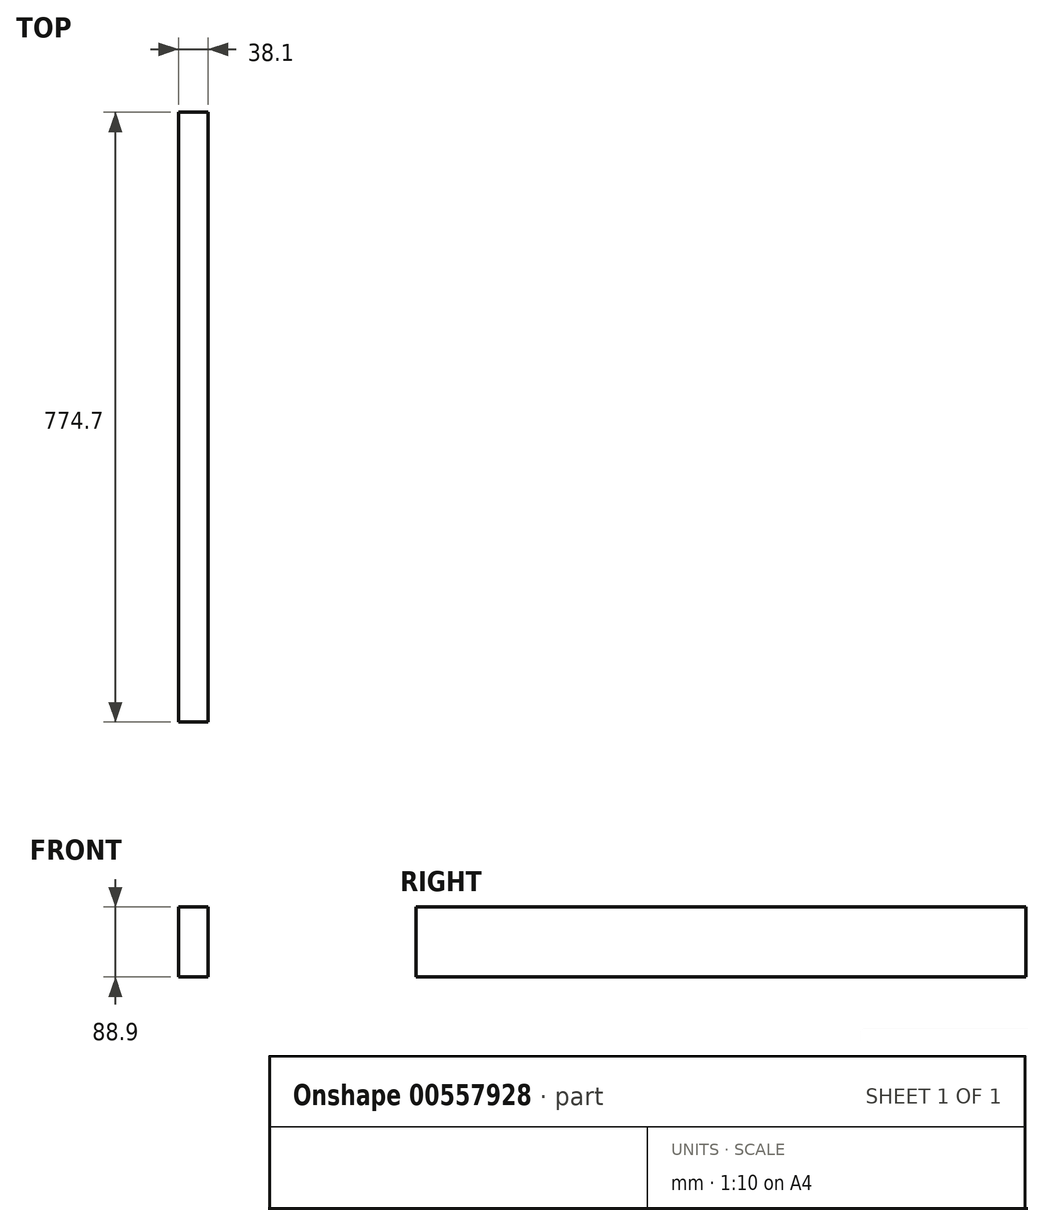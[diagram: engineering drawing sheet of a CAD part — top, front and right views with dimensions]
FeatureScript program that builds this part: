
annotation { "Feature Type Name" : "Feature", "Feature Type Description" : "" }
export const myFeature = defineFeature(function(context is Context, id is Id, definition is map)
    precondition{}
    {
        {
            var Q0;
            Q0=qCreatedBy(makeId("Right.planeOp"),FACE);
            var sketch = newSketch(context, id + "F0", { "sketchPlane" : qUnion([Q0])});
            skLineSegment(sketch, "E0.bottom", {"start": v(77.94, 175.26) * mm, "end": v(77.94, 86.36) * mm});
            skLineSegment(sketch, "E0.top", {"start": v(852.64, 175.26) * mm, "end": v(852.64, 86.36) * mm});
            skLineSegment(sketch, "E0.left", {"start": v(77.94, 175.26) * mm, "end": v(852.64, 175.26) * mm});
            skLineSegment(sketch, "E0.right", {"start": v(77.94, 86.36) * mm, "end": v(852.64, 86.36) * mm});
            skSolve(sketch);
        }
        {
            var Q0;
            Q0=makeQuery(id+"F0.imprint","IMPRINT",FACE,{"disambiguationData":[TD([[makeQuery(id+"F0.imprint","IMPRINT",EDGE,{"derivedFrom":sQuery(id+"F0.wireOp",EDGE,"E0.bottom")}),1.0]])]});
            extrude(context, id + "F1", {"entities" : qUnion([Q0]), "depth" : 38.1 * mm, "offsetDistance" : 25.4 * mm});
        }
    });
